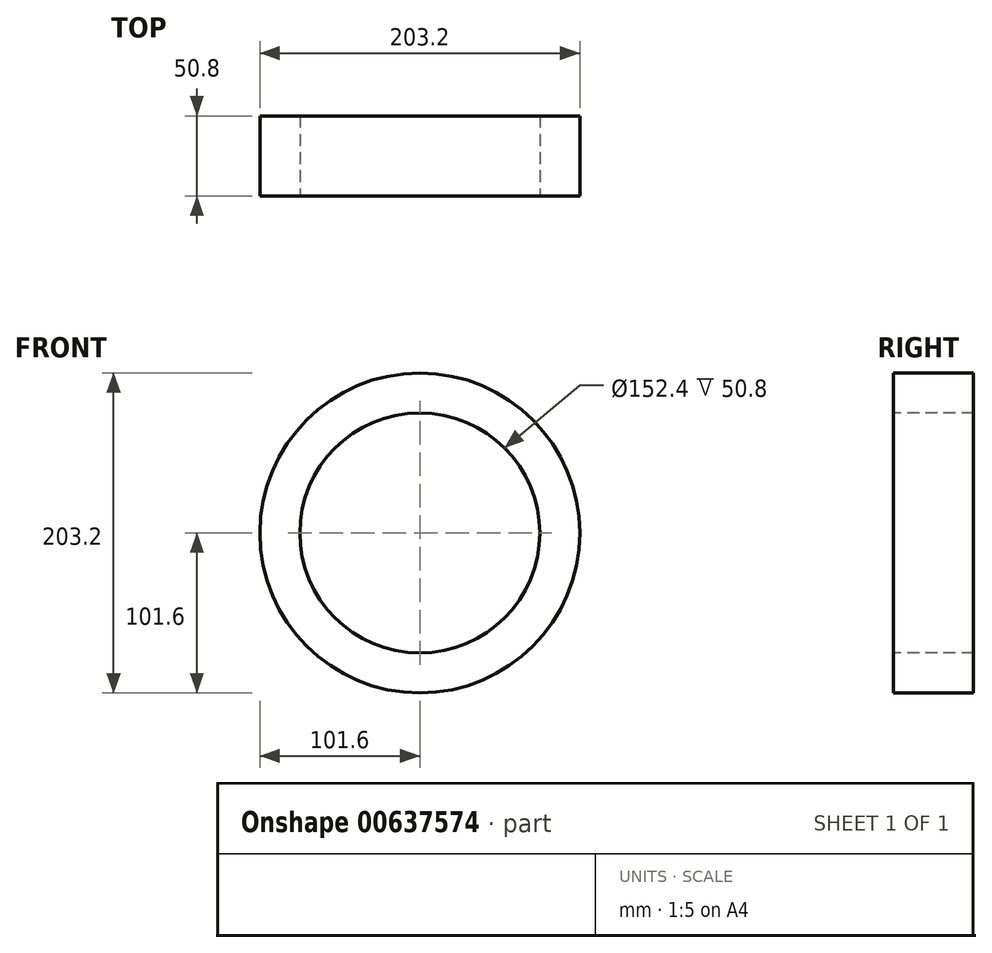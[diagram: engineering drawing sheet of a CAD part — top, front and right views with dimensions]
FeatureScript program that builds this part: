
annotation { "Feature Type Name" : "Feature", "Feature Type Description" : "" }
export const myFeature = defineFeature(function(context is Context, id is Id, definition is map)
    precondition{}
    {
        {
            var Q0;
            Q0=qCreatedBy(makeId("Top.planeOp"),FACE);
            var sketch = newSketch(context, id + "F0", { "sketchPlane" : qUnion([Q0])});
            skLineSegment(sketch, "E0.bottom", {"start": v(76.2, 0) * mm, "end": v(101.6, 0) * mm});
            skLineSegment(sketch, "E0.top", {"start": v(76.2, 50.8) * mm, "end": v(101.6, 50.8) * mm});
            skLineSegment(sketch, "E0.left", {"start": v(76.2, 0) * mm, "end": v(76.2, 50.8) * mm});
            skLineSegment(sketch, "E0.right", {"start": v(101.6, 0) * mm, "end": v(101.6, 50.8) * mm});
            skLineSegment(sketch, "E1", {"start": v(0, 0) * mm, "end": v(0, 108.63) * mm, "construction": true});
            skSolve(sketch);
        }
        {
            var Q0;
            Q0=makeQuery(id+"F0.imprint","IMPRINT",FACE,{"disambiguationData":[TD([[makeQuery(id+"F0.imprint","IMPRINT",EDGE,{"derivedFrom":sQuery(id+"F0.wireOp",EDGE,"E0.bottom")}),1.0]])]});
            var Q1;
            Q1=sQuery(id+"F0.wireOp",EDGE,"E1");
            revolve(context, id + "F1", {"entities" : qUnion([Q0]), "axis" : qUnion([Q1]), "revolveType" : RevolveType.FULL});
        }
    });
